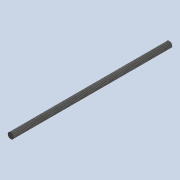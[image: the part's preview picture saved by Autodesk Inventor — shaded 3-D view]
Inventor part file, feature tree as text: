
AUTODESK INVENTOR PART (.ipt)
format: ipt  version: 2020 (Build 240168000, 168)  size: 82,944 bytes
history: native  units: mm
features: extrude x1, thread x1, sketch x1
ambient origin geometry x8: Origin, YZ Plane, XZ Plane, XY Plane, X Axis, Y Axis, Z Axis, Center Point
bodies: Solid1 (feature_tree)
feature tree (3):
  extrude  "Extrusion1"  Depth=210.0mm TaperAngle=0.0deg
  thread  "Thread1"  [1 undecoded]
  sketch  "Sketch1"  dims[d0=8.0mm d1=210.0mm d2=0.0mm d3=200.0mm d4=0.0mm]
note: 1 required parameter value undecoded (feature->parameter linkage not recoverable at this tier; creation-order binding heuristic only, values carry confidence <= 0.55)
